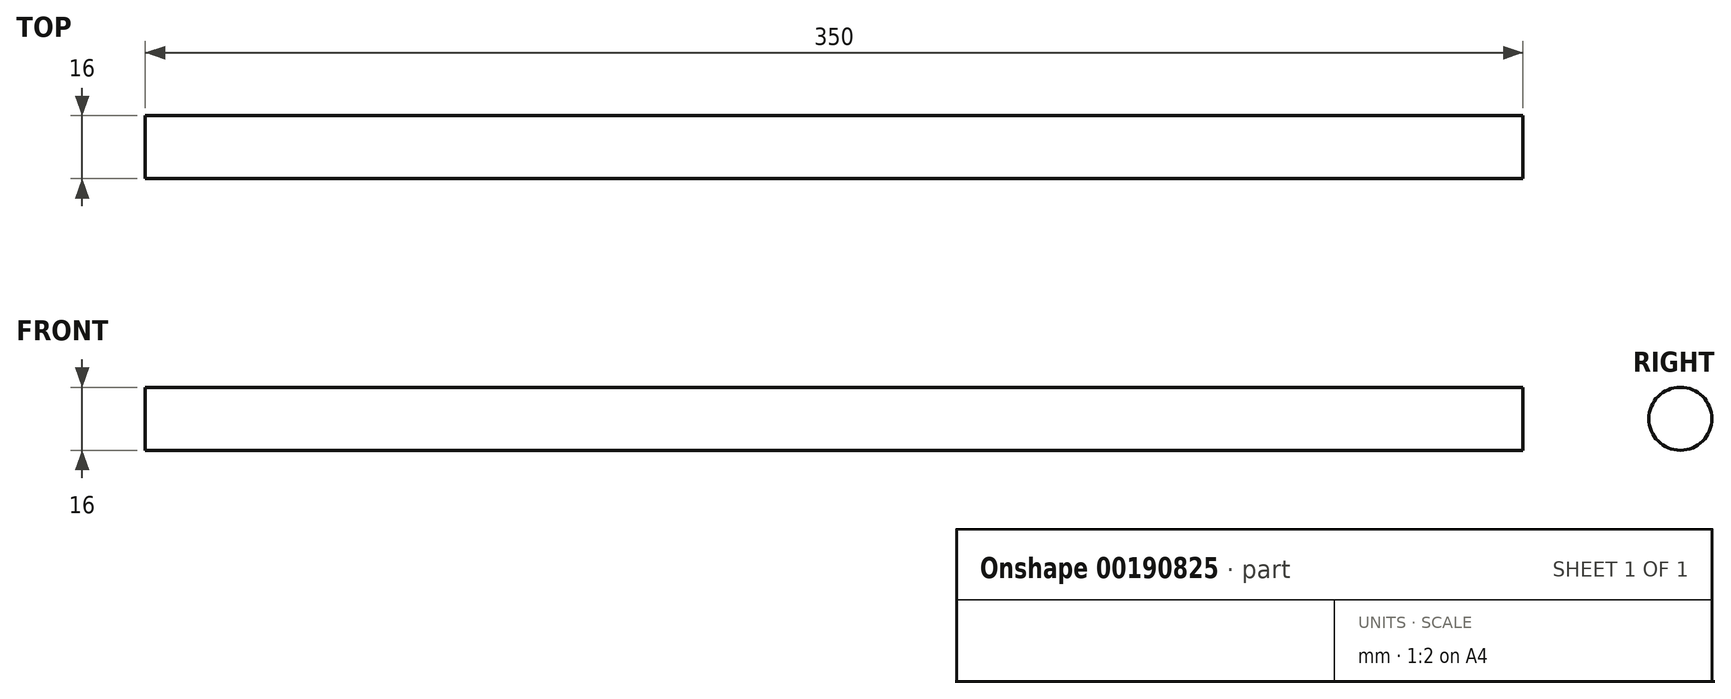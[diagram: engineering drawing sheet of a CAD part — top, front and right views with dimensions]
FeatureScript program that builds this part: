
annotation { "Feature Type Name" : "Feature", "Feature Type Description" : "" }
export const myFeature = defineFeature(function(context is Context, id is Id, definition is map)
    precondition{}
    {
        {
            var Q0;
            Q0=qCreatedBy(makeId("Front.planeOp"),FACE);
            var sketch = newSketch(context, id + "F0", { "sketchPlane" : qUnion([Q0])});
            skLineSegment(sketch, "E0", {"start": v(0, 0) * mm, "end": v(350, 0) * mm});
            skLineSegment(sketch, "E1", {"start": v(350, -16) * mm, "end": v(0, -16) * mm});
            skLineSegment(sketch, "E2", {"start": v(0, -16) * mm, "end": v(0, 0) * mm});
            skLineSegment(sketch, "E3", {"start": v(350, 0) * mm, "end": v(350, -16) * mm});
            skSolve(sketch);
        }
        {
            var Q0;
            Q0 = qSketchRegion(id + "F0", true);
            extrude(context, id + "F1", {"entities" : qUnion([Q0]), "depth" : 16 * mm});
        }
        {
            var Q0;
            Q0=makeQuery(id+"F1.opExtrude","CAP_EDGE",EDGE,{"disambiguationData":[OSD([sQuery(id+"F0.wireOp",EDGE,"E0")])],"isStart":false});
            var Q1;
            Q1=makeQuery(id+"F1.opExtrude","CAP_EDGE",EDGE,{"disambiguationData":[OSD([sQuery(id+"F0.wireOp",EDGE,"nbdqYXgJ-DodC-UVch-drDh-5jhUWvCHu4ym")])],"isStart":false});
            var Q2;
            Q2=makeQuery(id+"F1.opExtrude","CAP_EDGE",EDGE,{"disambiguationData":[OSD([sQuery(id+"F0.wireOp",EDGE,"wKio2eFU-EqMX-lnU3-cN6X-SMxGdcEBUQm3")])],"isStart":false});
            var Q3;
            Q3=makeQuery(id+"F1.opExtrude","CAP_EDGE",EDGE,{"disambiguationData":[OSD([sQuery(id+"F0.wireOp",EDGE,"IEZp8uMk-lge3-E2a7-4lWq-viO8wYBjzI6r")])],"isStart":false});
            var Q4;
            Q4=makeQuery(id+"F1.opExtrude","CAP_EDGE",EDGE,{"disambiguationData":[OSD([sQuery(id+"F0.wireOp",EDGE,"E1")])],"isStart":false});
            var Q5;
            Q5=makeQuery(id+"F1.opExtrude","CAP_EDGE",EDGE,{"disambiguationData":[OSD([sQuery(id+"F0.wireOp",EDGE,"7pSHU5r1-SP9S-3ucq-jiQJ-KswITb3SQqsv")])],"isStart":false});
            var Q6;
            Q6=makeQuery(id+"F1.opExtrude","CAP_EDGE",EDGE,{"disambiguationData":[OSD([sQuery(id+"F0.wireOp",EDGE,"7pSHU5r1-SP9S-3ucq-jiQJ-KswITb3SQqsv")])],"isStart":true});
            var Q7;
            Q7=makeQuery(id+"F1.opExtrude","CAP_EDGE",EDGE,{"disambiguationData":[OSD([sQuery(id+"F0.wireOp",EDGE,"wKio2eFU-EqMX-lnU3-cN6X-SMxGdcEBUQm3")])],"isStart":true});
            var Q8;
            Q8=makeQuery(id+"F1.opExtrude","CAP_EDGE",EDGE,{"disambiguationData":[OSD([sQuery(id+"F0.wireOp",EDGE,"nbdqYXgJ-DodC-UVch-drDh-5jhUWvCHu4ym")])],"isStart":true});
            var Q9;
            Q9=makeQuery(id+"F1.opExtrude","CAP_EDGE",EDGE,{"disambiguationData":[OSD([sQuery(id+"F0.wireOp",EDGE,"IEZp8uMk-lge3-E2a7-4lWq-viO8wYBjzI6r")])],"isStart":true});
            var Q10;
            Q10=makeQuery(id+"F1.opExtrude","CAP_EDGE",EDGE,{"disambiguationData":[OSD([sQuery(id+"F0.wireOp",EDGE,"E1")])],"isStart":true});
            var Q11;
            Q11=makeQuery(id+"F1.opExtrude","CAP_EDGE",EDGE,{"disambiguationData":[OSD([sQuery(id+"F0.wireOp",EDGE,"E0")])],"isStart":true});
            fillet(context, id + "F2", {"entities" : qUnion([Q0, Q1, Q2, Q3, Q4, Q5, Q6, Q7, Q8, Q9, Q10, Q11]), "radius" : 8 * mm, "allowEdgeOverflow" : false});
        }
    });
